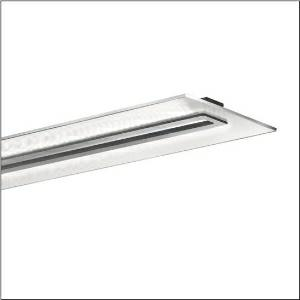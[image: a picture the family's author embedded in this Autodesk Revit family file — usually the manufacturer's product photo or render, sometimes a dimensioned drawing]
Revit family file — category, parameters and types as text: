
# Revit family: vega_r__11_5mn238dle003_bbe2
name_source: partatom
category: Lighting Fixtures
units: mm (PartAtom-declared; Revit-internal decimal feet)

## family parameters
Cut with Voids When Loaded = No
Host = Face
Light Source = No
Part Type = Normal
Room Calculation Point = No
Round Connector Dimension = Use Diameter
Shared = No

## types (1)
- --- (1 x LED 3000K / CRI = 80 (unbekannt), 7300 lm, 3000K)
    Apparent Load = 62 VA
    CIE Flux Codes = 61 86 97 62 100
    Color Rendering = 80
    Color Temperature = 3000K
    Default Elevation = 1800 mm
    Description = Vega® 11, office luminaire, primary light control with prismatic reflector, of PMMA, transparent prismatic structure, CAT 2 (L<= 1500cd/m²), light emission: direct/indirect distribution, primary light characteristic: symmetric, installation type: suspended mounting, surface-mounted, LED, rated luminous flux: 7.300lm, luminous efficacy: 118lm/W, light colour: 830, colour temperature: 3000K, control gear: DALI, with terminal, 3+2-pole, max. 2.5mm², mains connection: 230V, AC, 50Hz, connection cable inclusive, cable length: 1,5m, rated input power: 62W, luminaire housing, rectangular, rounded, of aluminium section, anodised, metallic grey (RAL 9006), length: 1.250mm, width: 350mm, height: 43mm, luminaire housing, lower part, of aluminium section, anodised, metallic grey (RAL 9006), of PC, grey, protection rating (complete): IP20, insulation class (complete): insulation class I (protective earthing), certification: CE, standard: EN 50419, packaging unit: 1 piece
    Height = 40 mm  [stored 0.131234 ft]
    Lamp = 1 x LED 3000K / CRI >= 80 (unbekannt)
    Lamp Light Flux = 7300 lm
    Lamp count = 1
    Length = 1250 mm
    Luminous efficacy = 118 lm/W
    Manufacturer = Siteco
    ModVariant = No
    Model = 5MN238DLE003
    Mounting Place = Ceiling
    Mounting Type = Pendant
    Number of Poles = 1
    OnlyDefault = Yes
    Power Factor = 1
    Product Name = Vega® 11
    Product group = office luminaire | ceiling pendant
    ProductGroupID = 904
    Protection Class = Protection class I
    Protection Degree = IP 20
    RLX_Detail_Level = 1
    RLX_Emergency_Light_Flux = 0 lm
    RLX_Emergency_Type = 0
    RLX_Emergency_Type_DB = No
    RlxData = <blob elided: 62825 chars, md5=07078835>
    Socket = socket
    Standby Power = 0 W
    System Light Flux = 7300 lm
    System Power = 62 W
    Type Comments = factory setting: luminous flux: 100 % | dim-lin: 254 | 460 mA
    Type Image = l_1004807.jpg
    URL = http://relux.com
    VarID = @adj_203892
    Voltage = 0 V
    Weight = 0.00 kg
    Width = 350 mm

note: [stored X ft] marks values corroborated as IEEE doubles in the binary element streams (Revit-internal decimal feet)

## geometry (parser evidence)
native form markers: Blend x4, Sweep x14
no freeform markers — native parametric forms only
